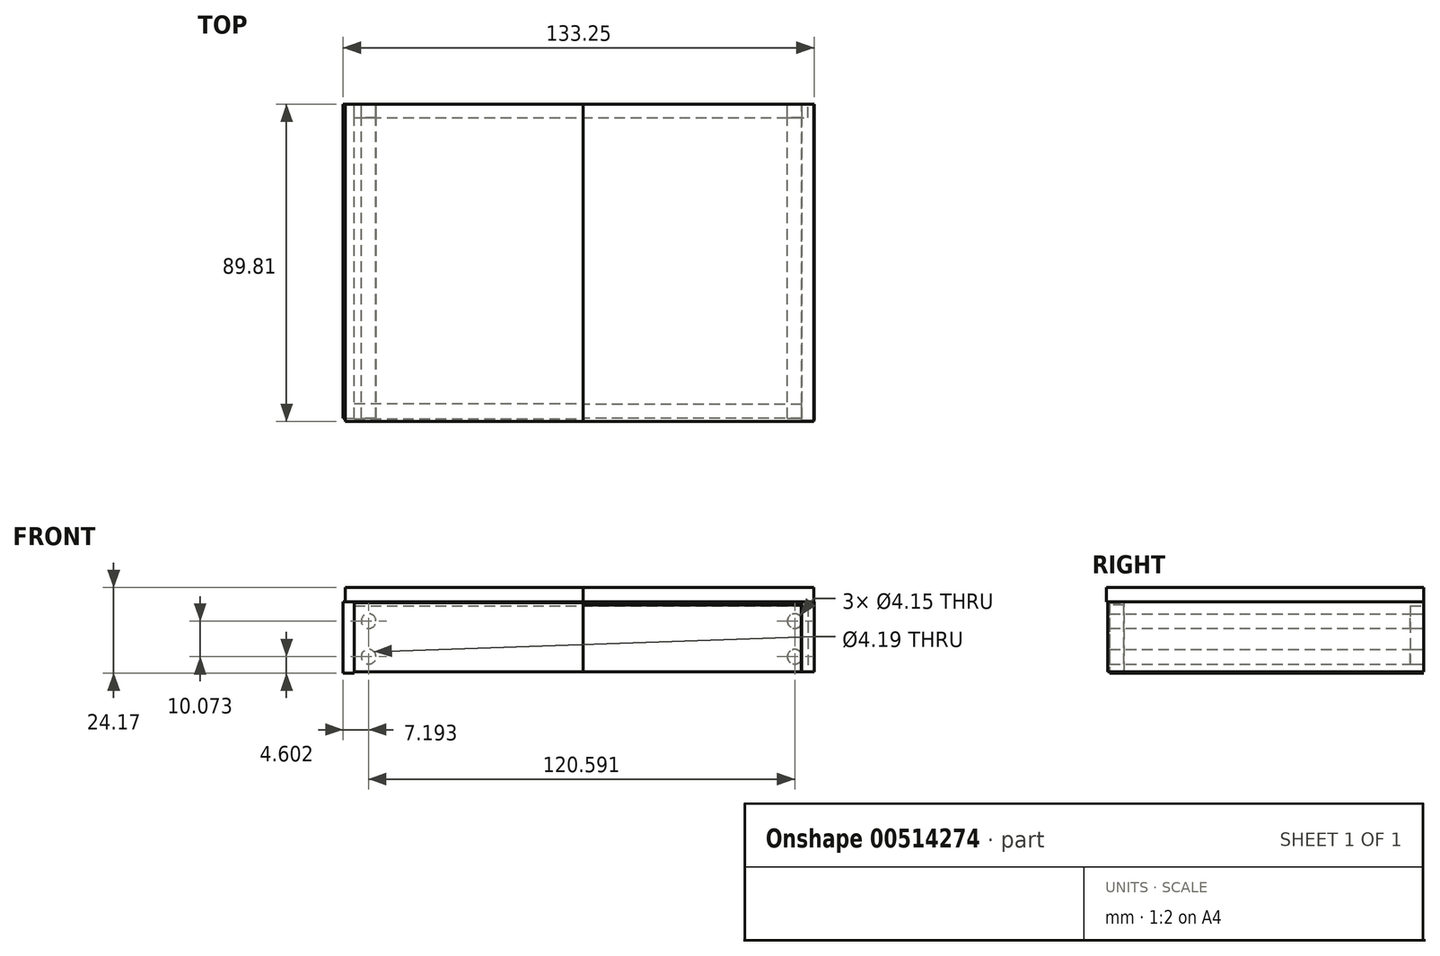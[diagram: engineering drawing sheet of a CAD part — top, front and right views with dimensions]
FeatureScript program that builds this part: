
annotation { "Feature Type Name" : "Feature", "Feature Type Description" : "" }
export const myFeature = defineFeature(function(context is Context, id is Id, definition is map)
    precondition{}
    {
        {
            var Q0;
            Q0=qCreatedBy(makeId("Front.planeOp"),FACE);
            var sketch = newSketch(context, id + "F0", { "sketchPlane" : qUnion([Q0])});
            skLineSegment(sketch, "E0.bottom", {"start": v(-64.76, 8.92) * mm, "end": v(63.6, 8.92) * mm});
            skLineSegment(sketch, "E0.top", {"start": v(-64.76, -9.79) * mm, "end": v(63.6, -9.79) * mm});
            skLineSegment(sketch, "E0.left", {"start": v(-64.76, 8.92) * mm, "end": v(-64.76, -9.79) * mm});
            skLineSegment(sketch, "E0.right", {"start": v(63.6, 8.92) * mm, "end": v(63.6, -9.79) * mm});
            skCircle(sketch, "E1", {"center": v(-60.73, 4.6) * mm, "radius": 2.08 * mm});
            skCircle(sketch, "E2", {"center": v(-60.73, -5.47) * mm, "radius": 2.1 * mm});
            skCircle(sketch, "E3", {"center": v(59.86, 4.6) * mm, "radius": 2.08 * mm});
            skCircle(sketch, "E4", {"center": v(59.86, -5.47) * mm, "radius": 2.08 * mm});
            skSolve(sketch);
        }
        {
            var Q0;
            Q0=makeQuery(id+"F0.imprint","IMPRINT",FACE,{"disambiguationData":[TD([[makeQuery(id+"F0.imprint","IMPRINT",EDGE,{"derivedFrom":sQuery(id+"F0.wireOp",EDGE,"E2")}),1.0]])]});
            var Q1;
            Q1=makeQuery(id+"F0.imprint","IMPRINT",FACE,{"disambiguationData":[TD([[makeQuery(id+"F0.imprint","IMPRINT",EDGE,{"derivedFrom":sQuery(id+"F0.wireOp",EDGE,"E1")}),1.0]])]});
            var Q2;
            Q2=makeQuery(id+"F0.imprint","IMPRINT",FACE,{"disambiguationData":[TD([[makeQuery(id+"F0.imprint","IMPRINT",EDGE,{"derivedFrom":sQuery(id+"F0.wireOp",EDGE,"E3")}),1.0]])]});
            var Q3;
            Q3=makeQuery(id+"F0.imprint","IMPRINT",FACE,{"disambiguationData":[TD([[makeQuery(id+"F0.imprint","IMPRINT",EDGE,{"derivedFrom":sQuery(id+"F0.wireOp",EDGE,"E4")}),1.0]])]});
            extrude(context, id + "F1", {"entities" : qUnion([Q0, Q1, Q2, Q3]), "depth" : 88.9 * mm});
        }
        {
            var Q0;
            Q0=qCreatedBy(makeId("Right.planeOp"),FACE);
            var sketch = newSketch(context, id + "F2", { "sketchPlane" : qUnion([Q0])});
            skLineSegment(sketch, "E5.bottom", {"start": v(0, 9.2) * mm, "end": v(-3.76, 9.2) * mm});
            skLineSegment(sketch, "E5.top", {"start": v(0, -9.79) * mm, "end": v(-3.76, -9.79) * mm});
            skLineSegment(sketch, "E5.left", {"start": v(0, 9.2) * mm, "end": v(0, -9.79) * mm});
            skLineSegment(sketch, "E5.right", {"start": v(-3.76, 9.2) * mm, "end": v(-3.76, -9.79) * mm});
            skLineSegment(sketch, "E6.bottom", {"start": v(-84.92, 9.2) * mm, "end": v(-88.95, 9.2) * mm});
            skLineSegment(sketch, "E6.top", {"start": v(-84.92, -9.79) * mm, "end": v(-88.95, -9.79) * mm});
            skLineSegment(sketch, "E6.left", {"start": v(-84.92, 9.2) * mm, "end": v(-84.92, -9.79) * mm});
            skLineSegment(sketch, "E6.right", {"start": v(-88.95, 9.2) * mm, "end": v(-88.95, -9.79) * mm});
            skSolve(sketch);
        }
        {
            var Q0;
            Q0=makeQuery(id+"F2.imprint","IMPRINT",FACE,{"disambiguationData":[TD([[makeQuery(id+"F2.imprint","IMPRINT",EDGE,{"derivedFrom":sQuery(id+"F2.wireOp",EDGE,"E6.bottom")}),1.0]])]});
            extrude(context, id + "F3", {"entities" : qUnion([Q0]), "depth" : 61.72 * mm});
        }
        {
            var Q0;
            Q0=qCreatedBy(makeId("Right.planeOp"),FACE);
            var sketch = newSketch(context, id + "F4", { "sketchPlane" : qUnion([Q0])});
            skLineSegment(sketch, "E7.bottom", {"start": v(-84.66, 9.79) * mm, "end": v(-88.98, 9.79) * mm});
            skLineSegment(sketch, "E7.top", {"start": v(-84.66, -9.79) * mm, "end": v(-88.98, -9.79) * mm});
            skLineSegment(sketch, "E7.left", {"start": v(-84.66, 9.79) * mm, "end": v(-84.66, -9.79) * mm});
            skLineSegment(sketch, "E7.right", {"start": v(-88.98, 9.79) * mm, "end": v(-88.98, -9.79) * mm});
            skSolve(sketch);
        }
        {
            var Q0;
            Q0=makeQuery(id+"F4.imprint","IMPRINT",FACE,{"disambiguationData":[TD([[makeQuery(id+"F4.imprint","IMPRINT",EDGE,{"derivedFrom":sQuery(id+"F4.wireOp",EDGE,"E7.bottom")}),1.0]])]});
            extrude(context, id + "F5", {"entities" : qUnion([Q0]), "oppositeDirection" : true, "depth" : 64.77 * mm});
        }
        {
            var Q0;
            Q0=qCreatedBy(makeId("Front.planeOp"),FACE);
            var sketch = newSketch(context, id + "F6", { "sketchPlane" : qUnion([Q0])});
            skLineSegment(sketch, "E8.bottom", {"start": v(-67.92, 10.07) * mm, "end": v(-64.76, 10.07) * mm});
            skLineSegment(sketch, "E8.top", {"start": v(-67.92, -10.07) * mm, "end": v(-64.76, -10.07) * mm});
            skLineSegment(sketch, "E8.left", {"start": v(-67.92, 10.07) * mm, "end": v(-67.92, -10.07) * mm});
            skLineSegment(sketch, "E8.right", {"start": v(-64.76, 10.07) * mm, "end": v(-64.76, -10.07) * mm});
            skLineSegment(sketch, "E9.bottom", {"start": v(61.88, 10.07) * mm, "end": v(65.33, 10.07) * mm});
            skLineSegment(sketch, "E9.top", {"start": v(61.88, -9.79) * mm, "end": v(65.33, -9.79) * mm});
            skLineSegment(sketch, "E9.left", {"start": v(61.88, 10.07) * mm, "end": v(61.88, -9.79) * mm});
            skLineSegment(sketch, "E9.right", {"start": v(65.33, 10.07) * mm, "end": v(65.33, -9.79) * mm});
            skSolve(sketch);
        }
        {
            var Q0;
            Q0=makeQuery(id+"F6.imprint","IMPRINT",FACE,{"disambiguationData":[TD([[makeQuery(id+"F6.imprint","IMPRINT",EDGE,{"derivedFrom":sQuery(id+"F6.wireOp",EDGE,"E8.bottom")}),-1.0]])]});
            extrude(context, id + "F7", {"entities" : qUnion([Q0]), "operationType" : NewBodyOperationType.ADD, "depth" : 88.9 * mm});
        }
        {
            var Q0;
            Q0=makeQuery(id+"F6.imprint","IMPRINT",FACE,{"disambiguationData":[TD([[makeQuery(id+"F6.imprint","IMPRINT",EDGE,{"derivedFrom":sQuery(id+"F6.wireOp",EDGE,"E9.bottom")}),-1.0]])]});
            extrude(context, id + "F8", {"entities" : qUnion([Q0]), "depth" : 89.4 * mm});
        }
        {
            var Q0;
            Q0=makeQuery(id+"F0.imprint","IMPRINT",FACE,{"disambiguationData":[TD([[makeQuery(id+"F0.imprint","IMPRINT",EDGE,{"derivedFrom":sQuery(id+"F0.wireOp",EDGE,"E0.bottom")}),-1.0]])]});
            extrude(context, id + "F9", {"entities" : qUnion([Q0]), "depth" : 3.8 * mm});
        }
        {
            var Q0;
            Q0=qCreatedBy(makeId("Right.planeOp"),FACE);
            var sketch = newSketch(context, id + "F10", { "sketchPlane" : qUnion([Q0])});
            skLineSegment(sketch, "E10.bottom", {"start": v(-89.81, 14.1) * mm, "end": v(0, 14.1) * mm});
            skLineSegment(sketch, "E10.top", {"start": v(-89.81, 10.07) * mm, "end": v(0, 10.07) * mm});
            skLineSegment(sketch, "E10.left", {"start": v(-89.81, 14.1) * mm, "end": v(-89.81, 10.07) * mm});
            skLineSegment(sketch, "E10.right", {"start": v(0, 14.1) * mm, "end": v(0, 10.07) * mm});
            skSolve(sketch);
        }
        {
            var Q0;
            Q0=makeQuery(id+"F10.imprint","IMPRINT",FACE,{"disambiguationData":[TD([[makeQuery(id+"F10.imprint","IMPRINT",EDGE,{"derivedFrom":sQuery(id+"F10.wireOp",EDGE,"E10.bottom")}),-1.0]])]});
            extrude(context, id + "F11", {"entities" : qUnion([Q0]), "operationType" : NewBodyOperationType.ADD, "depth" : 65.28 * mm});
        }
        {
            var Q0;
            Q0=makeQuery(id+"F11.opExtrude","CAP_FACE",FACE,{"disambiguationData":[OSD([sQuery(id+"F10.wireOp",EDGE,"E10.bottom"),sQuery(id+"F10.wireOp",EDGE,"E10.top"),sQuery(id+"F10.wireOp",EDGE,"E10.left"),sQuery(id+"F10.wireOp",EDGE,"E10.right")])],"isStart":false});
            extrude(context, id + "F12", {"entities" : qUnion([Q0]), "oppositeDirection" : true, "depth" : 132.6 * mm});
        }
    });
